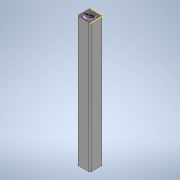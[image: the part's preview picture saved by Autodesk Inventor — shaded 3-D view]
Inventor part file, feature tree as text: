
AUTODESK INVENTOR PART (.ipt)
format: ipt  version: 2022 (Build 260153000, 153)  size: 124,416 bytes
history: native  units: in
note: dims shown in document units (in); Inventor stores cm internally (conversion verified against a paired STEP export)
features: extrude x3, sketch x2, fillet x2
ambient origin geometry x8: Origin, YZ Plane, XZ Plane, XY Plane, X Axis, Y Axis, Z Axis, Center Point
bodies: Solid1 (feature_tree)
feature tree (7):
  extrude  "Extrusion1"  Depth=3.937in
  sketch  "Sketch2"  dims[d2=39.3701in d3=0.0in d4=0.7874in d5=3.1496in d6=6.8898in d7=0.0in d8=0.1969in d9=0.0in d10=0.3937in d11=0.3937in]
  extrude  "Extrusion2"  Depth=0.3937in
  extrude  "Extrusion3"  Depth=0.3937in
  fillet  "Fillet1"  Radius=6.8898in
  fillet  "Fillet2"  Radius=0.1969in
  sketch  "Sketch1"  dims[d0=3.937in d1=3.937in]
